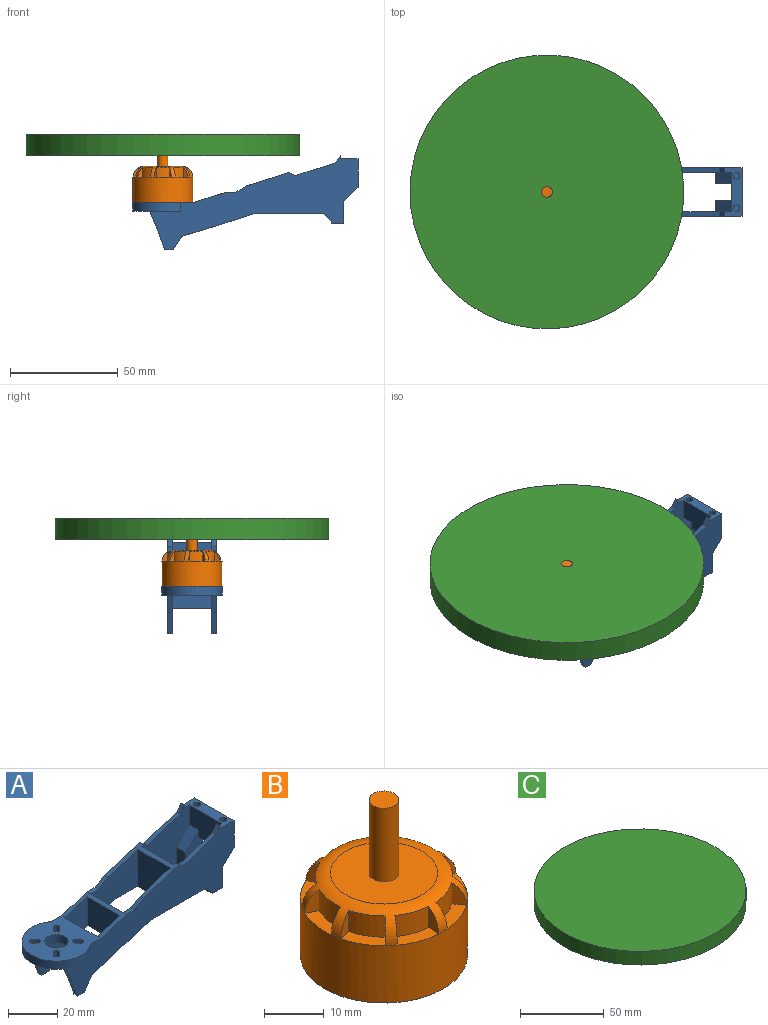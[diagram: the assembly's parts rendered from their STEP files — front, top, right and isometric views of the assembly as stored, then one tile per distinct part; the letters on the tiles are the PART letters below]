
ASSEMBLY  parts=3 mates=4
PART A: 83 faces, bbox 104.5x28x43.7 mm
  f0: plane 30.64x27.6mm, normal (0,1,0), area 504mm2, adj f5,f35,f36,f37,f42,f43,f44,f45
  f1: plane 27.04x22.51mm, normal (0,-1,0), area 400.2mm2, adj f34,f35,f47,f51,f52,f80,f81
  f2: plane 27.04x22.51mm, normal (0,1,0), area 400.2mm2, adj f34,f35,f47,f48,f49,f80,f81
  f3: plane 32.99x25.93mm, normal (0,-1,0), area 429.1mm2, adj f7,f8,f29,f34,f50,f62,f63,f64
  f4: plane 32.99x25.93mm, normal (0,1,0), area 429.1mm2, adj f7,f8,f29,f30,f31,f32,f33,f34
  f5: plane 18.5x13.34mm, normal (-1,0,0), area 209.2mm2, adj f0,f6,f42,f66,f71,f72,f73,f74
  f6: plane 7.78x5mm, normal (0,0,-1), area 38.9mm2, adj f5,f41,f72,f74
  f7: plane 18.5x4mm, normal (1,0,0), area 74mm2, adj f3,f4,f8,f29
  f8: plane 28x28mm, normal (0,0,-1), area 463.1mm2, adj f3,f4,f7,f9,f10,f11,f12,f13
  f9: cylinder r=1.25mm len=4mm, axis (0,0,-1), area 15.7mm2, adj f8,f10,f28,f29
  f10: plane 4x1.41mm, normal (-0.71,-0.71,0), area 8mm2, adj f8,f9,f11,f29
  f11: cylinder r=1.25mm len=4mm, axis (0,0,-1), area 15.7mm2, adj f8,f10,f28,f29
  f12: plane 96.63x43.7mm, normal (0,-1,0), area 1607mm2, adj f8,f23,f29,f30,f31,f32,f33,f34
  f13: plane 96.63x43.7mm, normal (0,1,0), area 1607mm2, adj f8,f23,f29,f34,f35,f41,f42,f47
  f14: cylinder r=1.25mm len=4mm, axis (0,0,-1), area 15.7mm2, adj f8,f15,f24,f29
  f15: plane 4x1.41mm, normal (-0.71,0.71,0), area 8mm2, adj f8,f14,f16,f29
  f16: cylinder r=1.25mm len=4mm, axis (0,0,-1), area 15.7mm2, adj f8,f15,f24,f29
  f17: cylinder r=1.25mm len=4mm, axis (0,0,-1), area 15.7mm2, adj f8,f18,f25,f29
  f18: plane 4x1.41mm, normal (0.71,0.71,0), area 8mm2, adj f8,f17,f19,f29
  f19: cylinder r=1.25mm len=4mm, axis (0,0,-1), area 15.7mm2, adj f8,f18,f25,f29
  f20: cylinder r=1.25mm len=4mm, axis (0,0,-1), area 15.7mm2, adj f8,f21,f26,f29
  f21: plane 4x1.41mm, normal (0.71,-0.71,0), area 8mm2, adj f8,f20,f22,f29
  f22: cylinder r=1.25mm len=4mm, axis (0,0,-1), area 15.7mm2, adj f8,f21,f26,f29
  f23: cylinder r=14mm len=28mm, axis (0,0,-1), area 247.3mm2, adj f8,f12,f13,f29
  f24: plane 4x1.41mm, normal (0.71,-0.71,0), area 8mm2, adj f8,f14,f16,f29
  f25: plane 4x1.41mm, normal (-0.71,-0.71,0), area 8mm2, adj f8,f17,f19,f29
  f26: plane 4x1.41mm, normal (-0.71,0.71,0), area 8mm2, adj f8,f20,f22,f29
  f27: cylinder r=4.75mm len=9.5mm, axis (0,0,-1), area 119.4mm2, adj f8,f29
  f28: plane 4x1.41mm, normal (0.71,0.71,0), area 8mm2, adj f8,f9,f11,f29
  f29: plane 28.32x28mm, normal (0,0,1), area 544.9mm2, adj f3,f4,f7,f9,f10,f11,f12,f13
  f30: plane 7.94x3.35mm, normal (-0.92,0,-0.39), area 17.2mm2, adj f4,f8,f12,f31
  f31: plane 10.06x3.56mm, normal (-0.94,0,-0.33), area 21.3mm2, adj f4,f12,f30,f32
  f32: plane 4.06x2mm, normal (0,0,-1), area 8.1mm2, adj f4,f12,f31,f33
  f33: plane 6.22x3.94mm, normal (0.84,0,-0.53), area 14.7mm2, adj f4,f12,f32,f34
  f34: plane 33.76x22.5mm, normal (0.3,0,-0.95), area 180.3mm2, adj f1,f2,f3,f4,f12,f13,f33,f35
  f35: plane 32.13x22.5mm, normal (0,0,-1), area 165.5mm2, adj f0,f1,f2,f12,f13,f34,f36,f61
  f36: plane 3.74x3.32mm, normal (-0.75,0,-0.66), area 10mm2, adj f0,f12,f35,f37
  f37: plane 12.76x7.36mm, normal (-1,0,0), area 69.9mm2, adj f0,f12,f36,f38,f73,f74
  f38: plane 7.36x6mm, normal (0,0,-1), area 37.1mm2, adj f12,f37,f39,f74,f77
  f39: plane 10.25x7.36mm, normal (1,0,0), area 75.4mm2, adj f12,f38,f40,f74
  f40: plane 7.36x6.5mm, normal (0.7,0,-0.71), area 67.2mm2, adj f12,f39,f41,f74
  f41: plane 22.5x13.34mm, normal (1,0,0), area 300mm2, adj f6,f12,f13,f40,f42,f57
  f42: plane 22.5x7.9mm, normal (0,0,1), area 110mm2, adj f0,f5,f12,f13,f41,f43,f56,f66
  f43: plane 2x1.4mm, normal (1,0,0), area 2.8mm2, adj f0,f12,f42,f44
  f44: plane 3.35x2.51mm, normal (-0.8,0,0.6), area 8.4mm2, adj f0,f12,f43,f45
  f45: plane 18.91x5.92mm, normal (-0.3,0,0.95), area 39.6mm2, adj f0,f12,f44,f46
  f46: plane 2.28x2mm, normal (0.56,0,0.83), area 5.5mm2, adj f0,f12,f45,f47
  f47: plane 22.5x20.16mm, normal (-0.3,0,0.95), area 123.3mm2, adj f0,f1,f2,f12,f13,f46,f48,f52
  f48: plane 5.38x3.18mm, normal (-0.51,0,0.86), area 12.5mm2, adj f2,f12,f47,f49
  f49: plane 4.5x2mm, normal (0.02,0,1), area 9mm2, adj f2,f12,f48,f50
  f50: plane 22.5x14.54mm, normal (-0.3,0,0.95), area 99.7mm2, adj f3,f4,f12,f13,f29,f49,f51,f79
  f51: plane 4.5x2mm, normal (0.02,0,1), area 9mm2, adj f1,f13,f50,f52
  f52: plane 5.38x3.18mm, normal (-0.51,0,0.86), area 12.5mm2, adj f1,f13,f47,f51
  f53: plane 2.28x2mm, normal (0.56,0,0.83), area 5.5mm2, adj f13,f47,f54,f66
  f54: plane 18.91x5.92mm, normal (-0.3,0,0.95), area 39.6mm2, adj f13,f53,f55,f66
  f55: plane 3.35x2.51mm, normal (-0.8,0,0.6), area 8.4mm2, adj f13,f54,f56,f66
  f56: plane 2x1.4mm, normal (1,0,0), area 2.8mm2, adj f13,f42,f55,f66
  f57: plane 7.36x6.5mm, normal (0.7,0,-0.71), area 67.2mm2, adj f13,f41,f58,f72
  f58: plane 10.25x7.36mm, normal (1,0,0), area 75.4mm2, adj f13,f57,f59,f72
  f59: plane 7.36x6mm, normal (0,0,-1), area 37.1mm2, adj f13,f58,f60,f72,f75
  f60: plane 12.76x7.36mm, normal (-1,0,0), area 69.9mm2, adj f13,f59,f61,f66,f71,f72
  f61: plane 3.74x3.32mm, normal (-0.75,0,-0.66), area 10mm2, adj f13,f35,f60,f66
  f62: plane 6.22x3.94mm, normal (0.84,0,-0.53), area 14.7mm2, adj f3,f13,f34,f63
  f63: plane 4.06x2mm, normal (0,0,-1), area 8.1mm2, adj f3,f13,f62,f64
  f64: plane 10.06x3.56mm, normal (-0.94,0,-0.33), area 21.3mm2, adj f3,f13,f63,f65
  f65: plane 7.94x3.35mm, normal (-0.92,0,-0.39), area 17.2mm2, adj f3,f8,f13,f64
  f66: plane 30.64x27.6mm, normal (0,-1,0), area 504mm2, adj f5,f35,f42,f47,f53,f54,f55,f56
  f67: cylinder r=1.5mm len=4mm, axis (0,0,1), area 37.7mm2, adj f42,f68
  f68: plane 3x3mm, normal (0,0,1), area 7.1mm2, adj f67
  f69: cylinder r=1.5mm len=4mm, axis (0,0,1), area 37.7mm2, adj f42,f70
  f70: plane 3x3mm, normal (0,0,1), area 7.1mm2, adj f69
  f71: plane 7.5x7.4mm, normal (-0.7,0,0.71), area 56.5mm2, adj f5,f60,f66,f72
  f72: plane 20.16x12.5mm, normal (0,-1,0), area 119.3mm2, adj f5,f6,f57,f58,f59,f60,f71
  f73: plane 7.5x7.4mm, normal (-0.7,0,0.71), area 56.5mm2, adj f0,f5,f37,f74
  f74: plane 20.16x12.5mm, normal (0,1,0), area 119.3mm2, adj f5,f6,f37,f38,f39,f40,f73
  f75: cylinder r=1.5mm len=4mm, axis (0,0,-1), area 37.7mm2, adj f59,f76
  f76: plane 3x3mm, normal (0,0,-1), area 7.1mm2, adj f75
  f77: cylinder r=1.5mm len=4mm, axis (0,0,-1), area 37.7mm2, adj f38,f78
  f78: plane 3x3mm, normal (0,0,-1), area 7.1mm2, adj f77
  f79: plane 18.5x14.04mm, normal (-1,0,0), area 259.8mm2, adj f3,f4,f34,f50
  f80: plane 18.5x14.04mm, normal (1,0,0), area 259.8mm2, adj f1,f2,f34,f50
  f81: plane 18.5x18.22mm, normal (-1,0,0), area 337.2mm2, adj f1,f2,f35,f47
  f82: plane 18.85x18.5mm, normal (1,0,0), area 348.7mm2, adj f0,f35,f47,f66
PART B: 42 faces, bbox 30.2x30.2x31.7 mm
  f0: torus R=8.95mm, axis (0,0,1), area 256.7mm2, adj f1,f2,f4,f5,f6,f8,f9,f10
  f1: cylinder r=13.95mm len=27.9mm, axis (0,0,-1), area 1025.5mm2, adj f0,f3,f7,f11,f15,f19,f23,f27
  f2: plane 17.9x17.9mm, normal (0,0,1), area 232mm2, adj f0,f40
  f3: plane 27.9x27.9mm, normal (0,0,-1), area 611.4mm2, adj f1
  f4: plane 4.33x2.4mm, normal (-0.96,0.27,0), area 7.7mm2, adj f0,f6,f7
  f5: plane 4.33x2.4mm, normal (0.96,0.27,0), area 7.7mm2, adj f0,f6,f7
  f6: cylinder r=11.45mm len=6.27mm, axis (0,0,1), area 27.5mm2, adj f0,f4,f5,f7
  f7: plane 7.64x2.94mm, normal (0,0,1), area 17.6mm2, adj f1,f4,f5,f6
  f8: plane 4.33x2.07mm, normal (0.56,0.83,0), area 7.7mm2, adj f0,f9,f11
  f9: cylinder r=11.45mm len=4.8mm, axis (0,0,1), area 27.5mm2, adj f0,f8,f10,f11
  f10: plane 4.33x2.28mm, normal (-0.91,-0.41,0), area 7.7mm2, adj f0,f9,f11
  f11: plane 6.87x6.31mm, normal (0,0,1), area 17.6mm2, adj f1,f8,f9,f10
  f12: plane 4.33x2.49mm, normal (-0.1,0.99,0), area 7.7mm2, adj f0,f13,f15
  f13: cylinder r=11.45mm len=6.17mm, axis (0,0,1), area 27.5mm2, adj f0,f12,f14,f15
  f14: plane 4.33x2.25mm, normal (-0.44,-0.9,0), area 7.7mm2, adj f0,f13,f15
  f15: plane 7.52x3.65mm, normal (0,0,1), area 17.6mm2, adj f1,f12,f13,f14
  f16: plane 4.33x2.49mm, normal (-1,0.07,0), area 7.7mm2, adj f0,f17,f19
  f17: cylinder r=11.45mm len=5.89mm, axis (0,0,1), area 27.5mm2, adj f0,f16,f18,f19
  f18: plane 4.33x2.03mm, normal (0.81,-0.59,0), area 7.7mm2, adj f0,f17,f19
  f19: plane 7.36x4.64mm, normal (0,0,1), area 17.6mm2, adj f1,f16,f17,f18
  f20: plane 4.33x1.8mm, normal (-0.72,0.7,0), area 7.7mm2, adj f0,f21,f23
  f21: cylinder r=11.45mm len=5.43mm, axis (0,0,1), area 27.5mm2, adj f0,f20,f22,f23
  f22: plane 4.33x2.42mm, normal (0.24,-0.97,0), area 7.7mm2, adj f0,f21,f23
  f23: plane 7.22x5.56mm, normal (0,0,1), area 17.6mm2, adj f1,f20,f21,f22
  f24: plane 4.33x2.42mm, normal (-0.24,-0.97,0), area 7.7mm2, adj f0,f25,f27
  f25: cylinder r=11.45mm len=5.43mm, axis (0,0,1), area 27.5mm2, adj f0,f24,f26,f27
  f26: plane 4.33x1.8mm, normal (0.72,0.7,0), area 7.7mm2, adj f0,f25,f27
  f27: plane 7.22x5.56mm, normal (0,0,1), area 17.6mm2, adj f1,f24,f25,f26
  f28: plane 4.33x2.03mm, normal (-0.81,-0.59,0), area 7.7mm2, adj f0,f29,f31
  f29: cylinder r=11.45mm len=5.89mm, axis (0,0,1), area 27.5mm2, adj f0,f28,f30,f31
  f30: plane 4.33x2.49mm, normal (1,0.07,0), area 7.7mm2, adj f0,f29,f31
  f31: plane 7.36x4.64mm, normal (0,0,1), area 17.6mm2, adj f1,f28,f29,f30
  f32: plane 4.33x2.25mm, normal (0.44,-0.9,0), area 7.7mm2, adj f0,f33,f35
  f33: cylinder r=11.45mm len=6.17mm, axis (0,0,1), area 27.5mm2, adj f0,f32,f34,f35
  f34: plane 4.33x2.49mm, normal (0.1,0.99,0), area 7.7mm2, adj f0,f33,f35
  f35: plane 7.52x3.65mm, normal (0,0,1), area 17.6mm2, adj f1,f32,f33,f34
  f36: plane 4.33x2.28mm, normal (0.91,-0.41,0), area 7.7mm2, adj f0,f37,f39
  f37: cylinder r=11.45mm len=4.8mm, axis (0,0,1), area 27.5mm2, adj f0,f36,f38,f39
  f38: plane 4.33x2.07mm, normal (-0.56,0.83,0), area 7.7mm2, adj f0,f37,f39
  f39: plane 6.87x6.31mm, normal (0,0,1), area 17.6mm2, adj f1,f36,f37,f38
  f40: cylinder r=2.5mm len=15mm, axis (0,0,-1), area 235.6mm2, adj f2,f41
  f41: plane 5x5mm, normal (0,0,1), area 19.6mm2, adj f40
PART C: 3 faces, bbox 127x127x10 mm
  f0: cylinder r=63.5mm len=127mm, axis (0,0,-1), area 3989.8mm2, adj f1,f2
  f1: plane 127x127mm, normal (0,0,1), area 12667.7mm2, adj f0
  f2: plane 127x127mm, normal (0,0,-1), area 12667.7mm2, adj f0
PLACE A t=(0,0,18)mm
PLACE B rot(axis=(0,0,1),180deg) t=(0,0,22)mm
PLACE C rot(axis=(0,0,1),137.4deg) t=(0,0,43.7)mm
MATE planar B.f0 <-> A.f23  axis (0,0,-1) through (0,0,22)mm
MATE planar C.f0 <-> B.f0  axis (0,0,1) through (0,0,53.7)mm
MATE cylindrical C.f0 <-> B.f0  axis (0,0,1) through (0,0,53.7)mm
MATE cylindrical B.f0 <-> A.f23  axis (0,0,-1) through (0,0,22)mm
